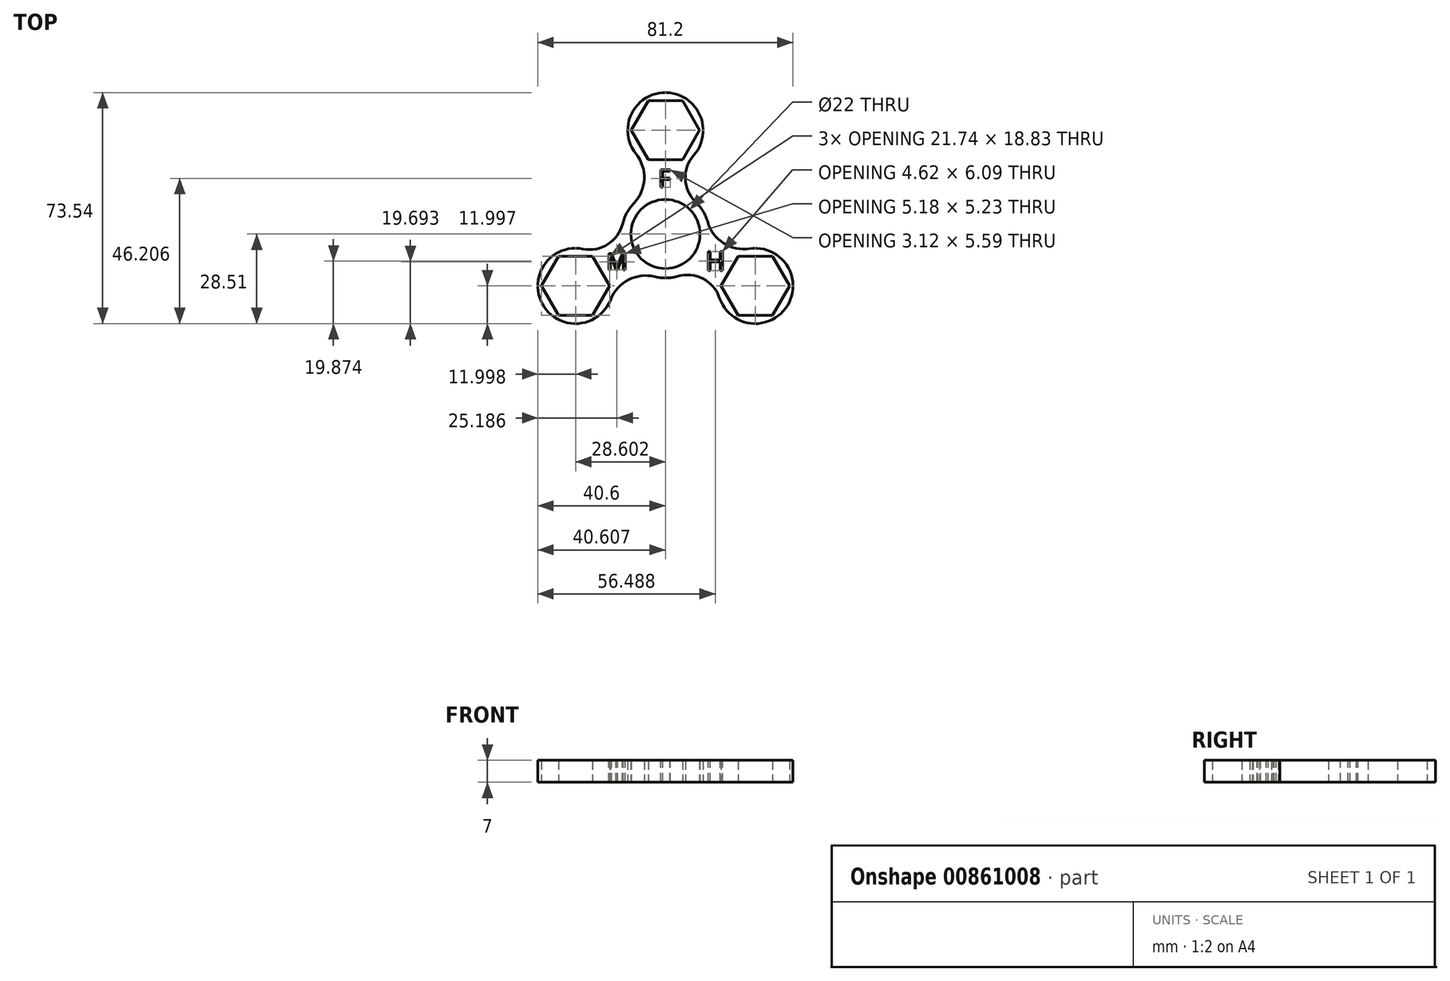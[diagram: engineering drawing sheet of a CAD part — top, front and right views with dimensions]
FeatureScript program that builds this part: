
annotation { "Feature Type Name" : "Feature", "Feature Type Description" : "" }
export const myFeature = defineFeature(function(context is Context, id is Id, definition is map)
    precondition{}
    {
        {
            var Q0;
            Q0=qCreatedBy(makeId("Top.planeOp"),FACE);
            var sketch = newSketch(context, id + "F0", { "sketchPlane" : qUnion([Q0])});
            skCircle(sketch, "E0", {"center": v(0, 0) * mm, "radius": 11 * mm});
            skCircle(sketch, "E1", {"center": v(0, 0) * mm, "radius": 45.03 * mm, "construction": true});
            skCircle(sketch, "E2", {"center": v(0, 0) * mm, "radius": 14 * mm});
            skCircle(sketch, "E3", {"center": v(0, 33.03) * mm, "radius": 12 * mm});
            skArc(sketch, "E4", {"start": v(-10.07, 9.73) * mm, "mid": v(-6.73, 17.48) * mm, "end": v(-9.35, 25.5) * mm});
            skArc(sketch, "E5", {"start": v(9.03, 25.12) * mm, "mid": v(6.35, 17.48) * mm, "end": v(9.69, 10.1) * mm});
            skCircle(sketch, "E6.1.1", {"center": v(-28.6, -16.51) * mm, "radius": 12 * mm});
            skArc(sketch, "E6.1.2", {"start": v(-3.39, -13.58) * mm, "mid": v(-11.78, -14.57) * mm, "end": v(-17.41, -20.85) * mm});
            skArc(sketch, "E6.1.3", {"start": v(-26.27, -4.74) * mm, "mid": v(-18.31, -3.24) * mm, "end": v(-13.6, 3.34) * mm});
            skCircle(sketch, "E6.2.1", {"center": v(28.6, -16.51) * mm, "radius": 12 * mm});
            skArc(sketch, "E6.2.2", {"start": v(13.46, 3.86) * mm, "mid": v(18.5, -2.91) * mm, "end": v(26.76, -4.65) * mm});
            skArc(sketch, "E6.2.3", {"start": v(17.24, -20.38) * mm, "mid": v(11.97, -14.24) * mm, "end": v(3.9, -13.44) * mm});
            skCircle(sketch, "E7.cCircle", {"center": v(0, 33.03) * mm, "radius": 9.42 * mm, "construction": true});
            skLineSegment(sketch, "E7.0", {"start": v(5.44, 23.61) * mm, "end": v(-5.44, 23.61) * mm});
            skLineSegment(sketch, "E7.1", {"start": v(-5.44, 23.61) * mm, "end": v(-10.87, 33.03) * mm});
            skLineSegment(sketch, "E7.2", {"start": v(-10.87, 33.03) * mm, "end": v(-5.44, 42.44) * mm});
            skLineSegment(sketch, "E7.3", {"start": v(-5.44, 42.44) * mm, "end": v(5.44, 42.44) * mm});
            skLineSegment(sketch, "E7.4", {"start": v(5.44, 42.44) * mm, "end": v(10.87, 33.03) * mm});
            skLineSegment(sketch, "E7.5", {"start": v(10.87, 33.03) * mm, "end": v(5.44, 23.61) * mm});
            skPoint(sketch, "E7.0.midPoint", {"position": v(0, 23.61) * mm});
            skCircle(sketch, "E8.1.0", {"center": v(-28.6, -16.51) * mm, "radius": 9.42 * mm, "construction": true});
            skLineSegment(sketch, "E8.1.1", {"start": v(-34.04, -25.93) * mm, "end": v(-39.47, -16.51) * mm});
            skLineSegment(sketch, "E8.1.2", {"start": v(-39.47, -16.51) * mm, "end": v(-34.04, -7.1) * mm});
            skLineSegment(sketch, "E8.1.3", {"start": v(-34.04, -7.1) * mm, "end": v(-23.17, -7.1) * mm});
            skLineSegment(sketch, "E8.1.4", {"start": v(-23.17, -7.1) * mm, "end": v(-17.73, -16.51) * mm});
            skLineSegment(sketch, "E8.1.5", {"start": v(-17.73, -16.51) * mm, "end": v(-23.17, -25.93) * mm});
            skLineSegment(sketch, "E8.1.6", {"start": v(-23.17, -25.93) * mm, "end": v(-34.04, -25.93) * mm});
            skCircle(sketch, "E8.2.0", {"center": v(28.6, -16.51) * mm, "radius": 9.42 * mm, "construction": true});
            skLineSegment(sketch, "E8.2.1", {"start": v(39.47, -16.51) * mm, "end": v(34.04, -25.93) * mm});
            skLineSegment(sketch, "E8.2.2", {"start": v(34.04, -25.93) * mm, "end": v(23.17, -25.93) * mm});
            skLineSegment(sketch, "E8.2.3", {"start": v(23.17, -25.93) * mm, "end": v(17.73, -16.51) * mm});
            skLineSegment(sketch, "E8.2.4", {"start": v(17.73, -16.51) * mm, "end": v(23.17, -7.1) * mm});
            skLineSegment(sketch, "E8.2.5", {"start": v(23.17, -7.1) * mm, "end": v(34.04, -7.1) * mm});
            skLineSegment(sketch, "E8.2.6", {"start": v(34.04, -7.1) * mm, "end": v(39.47, -16.51) * mm});
            skSolve(sketch);
        }
        {
            var Q0;
            {var subQ0=sQuery(id+"F0.wireOp",EDGE,"E4");Q0=makeQuery(id+"F0.imprint","IMPRINT",FACE,{"disambiguationData":[TD([[makeQuery(id+"F0.imprint","IMPRINT",EDGE,{"derivedFrom":subQ0}),-1.0]])]});}
            var Q1;
            Q1=makeQuery(id+"F0.imprint","IMPRINT",FACE,{"disambiguationData":[TD([[makeQuery(id+"F0.imprint","IMPRINT",EDGE,{"derivedFrom":sQuery(id+"F0.wireOp",EDGE,"E0")}),-1.0]])]});
            var Q2;
            {var subQ0=sQuery(id+"F0.wireOp",EDGE,"E6.1.2");Q2=makeQuery(id+"F0.imprint","IMPRINT",FACE,{"disambiguationData":[TD([[makeQuery(id+"F0.imprint","IMPRINT",EDGE,{"derivedFrom":subQ0}),-1.0]])]});}
            var Q3;
            {var subQ0=sQuery(id+"F0.wireOp",EDGE,"E6.2.2");Q3=makeQuery(id+"F0.imprint","IMPRINT",FACE,{"disambiguationData":[TD([[makeQuery(id+"F0.imprint","IMPRINT",EDGE,{"derivedFrom":subQ0}),-1.0]])]});}
            var Q4;
            Q4=makeQuery(id+"F0.imprint","IMPRINT",FACE,{"disambiguationData":[TD([[makeQuery(id+"F0.imprint","IMPRINT",EDGE,{"derivedFrom":sQuery(id+"F0.wireOp",EDGE,"E7.0")}),1.0]])]});
            var Q5;
            Q5=makeQuery(id+"F0.imprint","IMPRINT",FACE,{"disambiguationData":[TD([[makeQuery(id+"F0.imprint","IMPRINT",EDGE,{"derivedFrom":sQuery(id+"F0.wireOp",EDGE,"E8.1.1")}),1.0]])]});
            var Q6;
            Q6=makeQuery(id+"F0.imprint","IMPRINT",FACE,{"disambiguationData":[TD([[makeQuery(id+"F0.imprint","IMPRINT",EDGE,{"derivedFrom":sQuery(id+"F0.wireOp",EDGE,"E8.2.1")}),1.0]])]});
            extrude(context, id + "F1", {"entities" : qUnion([Q0, Q1, Q2, Q3, Q4, Q5, Q6]), "depth" : 7 * mm, "offsetDistance" : 25 * mm, "symmetric" : true});
        }
        {
            var Q0;
            Q0=makeQuery(id+"F1.opExtrude","CAP_FACE",FACE,{"disambiguationData":[OSD([sQuery(id+"F0.wireOp",EDGE,"E0"),sQuery(id+"F0.wireOp",EDGE,"E2"),sQuery(id+"F0.wireOp",EDGE,"E3"),sQuery(id+"F0.wireOp",EDGE,"E4"),sQuery(id+"F0.wireOp",EDGE,"E5"),sQuery(id+"F0.wireOp",EDGE,"E6.1.1"),sQuery(id+"F0.wireOp",EDGE,"E6.1.2"),sQuery(id+"F0.wireOp",EDGE,"E6.1.3"),sQuery(id+"F0.wireOp",EDGE,"E6.2.1"),sQuery(id+"F0.wireOp",EDGE,"E6.2.2"),sQuery(id+"F0.wireOp",EDGE,"E6.2.3"),sQuery(id+"F0.wireOp",EDGE,"E7.0"),sQuery(id+"F0.wireOp",EDGE,"E7.1"),sQuery(id+"F0.wireOp",EDGE,"E7.2"),sQuery(id+"F0.wireOp",EDGE,"E7.3"),sQuery(id+"F0.wireOp",EDGE,"E7.4"),sQuery(id+"F0.wireOp",EDGE,"E7.5"),sQuery(id+"F0.wireOp",EDGE,"E8.1.1"),sQuery(id+"F0.wireOp",EDGE,"E8.1.2"),sQuery(id+"F0.wireOp",EDGE,"E8.1.3"),sQuery(id+"F0.wireOp",EDGE,"E8.1.4"),sQuery(id+"F0.wireOp",EDGE,"E8.1.5"),sQuery(id+"F0.wireOp",EDGE,"E8.1.6"),sQuery(id+"F0.wireOp",EDGE,"E8.2.1"),sQuery(id+"F0.wireOp",EDGE,"E8.2.2"),sQuery(id+"F0.wireOp",EDGE,"E8.2.3"),sQuery(id+"F0.wireOp",EDGE,"E8.2.4"),sQuery(id+"F0.wireOp",EDGE,"E8.2.5"),sQuery(id+"F0.wireOp",EDGE,"E8.2.6")])],"isStart":false});
            var sketch = newSketch(context, id + "F2", { "sketchPlane" : qUnion([Q0])});
            skText(sketch, "E9", { "text": "F", "fontName": "OpenSans-Regular.ttf"});
            skText(sketch, "E10", { "text": "M", "fontName": "OpenSans-Regular.ttf"});
            skText(sketch, "E11", { "text": "H", "fontName": "OpenSans-Regular.ttf"});
            const initialGuessF2  = {"E9": [-0.00232, 0.0149, 1, 0, 0.00564], "E10": [-0.01872, -0.01143, 1, 0, 0.00527], "E11": [0.01274, -0.01168, 1, 0, 0.00614]};
            skSetInitialGuess(sketch, initialGuessF2);
            skSolve(sketch);
        }
        {
            var Q0;
            Q0 = qSketchRegion(id + "F2", true);
            extrude(context, id + "F3", {"entities" : qUnion([Q0]), "operationType" : NewBodyOperationType.REMOVE, "oppositeDirection" : true, "depth" : 25 * mm, "offsetDistance" : 25 * mm});
        }
    });
